# Revit family: TIRA LED 8MM24V_SL12024.U_W_N_C
name_source: partatom
category: Luminarias
units: mm (PartAtom-declared; Revit-internal decimal feet)

## family parameters
Compartido = No
Corte con vacíos al cargar = No
Cota de conector redondo = Diámetro de uso
Origen de luz = Sí
Punto de cálculo de habitación = No
Se basa en plano de trabajo = Sí
Siempre vertical = No
Tipo de pieza = Normal

## types (5) — shared parameters
Cambio de temperatura de color de luz atenuada = <Ninguno>
Comentarios de vataje = 24
Fabricante = BRILLANT
Filtro de color = 16777215
Longitud de línea de emisión = 600 mm
Marca = BRILLANT
Modelo Lampara = 3014 SMD
Tamaño de símbolo de origen de luz = 610 mm
zero-valued in all types: Elevación por defecto

## per-type parameters (varying)
| type | Descripción | Modelo |
| TIRA LED 8MM24V_SL12024.U | TIRA LED 8MM MONOCROMATICA , CON UNA POTENCIA DE 9.6W/M DE UN TIPO DE LED 3014 SMD, USO PARA INTERIORES COMO EXTERIORES IP20-65, IRC80, 120 LEDS POR METRO, PRESENTACION DE 5M, CORTE 5CM, TEMPERATURA EN BLANCO ULTRA CALIDO 2400K, 848 LUMENES POR METRO, AMPERAJE DE 0.35A, ALIMENTADO A 24V, REQUIERE ACCESORIOS. | SL12024.U |
| TIRA LED 8MM24V_SL12024.UU | TIRA LED 8MM MONOCROMATICA , CON UNA POTENCIA DE 9.6W/M DE UN TIPO DE LED 3014 SMD, USO PARA INTERIORES COMO EXTERIORES IP20-65, IRC80, 120 LEDS POR METRO, PRESENTACION DE 5M, CORTE 5CM, TEMPERATURA EN BLANCO CALIDO 2700K, 894 LUMENES POR METRO, AMPERAJE DE 0.35A, ALIMENTADO A 24V, REQUIERE ACCESORIOS. | SL12024.UU |
| TIRA LED 8MM24V_SL12024.W | TIRA LED 8MM MONOCROMATICA , CON UNA POTENCIA DE 9.6W/M DE UN TIPO DE LED 3014 SMD, USO PARA INTERIORES COMO EXTERIORES IP20-65, IRC80, 120 LEDS POR METRO, PRESENTACION DE 5M, CORTE 5CM, TEMPERATURA EN BLANCO CALIDO 3000K, 894 LUMENES POR METRO, AMPERAJE DE 0.35A, ALIMENTADO A 24V, REQUIERE ACCESORIOS. | SL12024.W |
| TIRA LED 8MM24V_SL12024.N | TIRA LED 8MM MONOCROMATICA , CON UNA POTENCIA DE 9.6W/M DE UN TIPO DE LED 3014 SMD, USO PARA INTERIORES COMO EXTERIORES IP20-65, IRC80, 120 LEDS POR METRO, PRESENTACION DE 5M, CORTE 5CM, TEMPERATURA EN BLANCO FRIO 4000K, 921 LUMENES POR METRO, AMPERAJE DE 0.35A, ALIMENTADO A 24V, REQUIERE ACCESORIOS. | SL12024.N |
| TIRA LED 8MM24V_SL12024.C | TIRA LED 8MM MONOCROMATICA , CON UNA POTENCIA DE 9.6W/M DE UN TIPO DE LED 3014 SMD, USO PARA INTERIORES COMO EXTERIORES IP20-65, IRC80, 120 LEDS POR METRO, PRESENTACION DE 5M, CORTE 5CM, TEMPERATURA EN BLANCO FRIO 6500K, 894 LUMENES POR METRO, AMPERAJE DE 0.35A, ALIMENTADO A 24V, REQUIERE ACCESORIOS. | SL12024.C |

## geometry (parser evidence)
native form markers: Blend x2
no freeform markers — native parametric forms only
